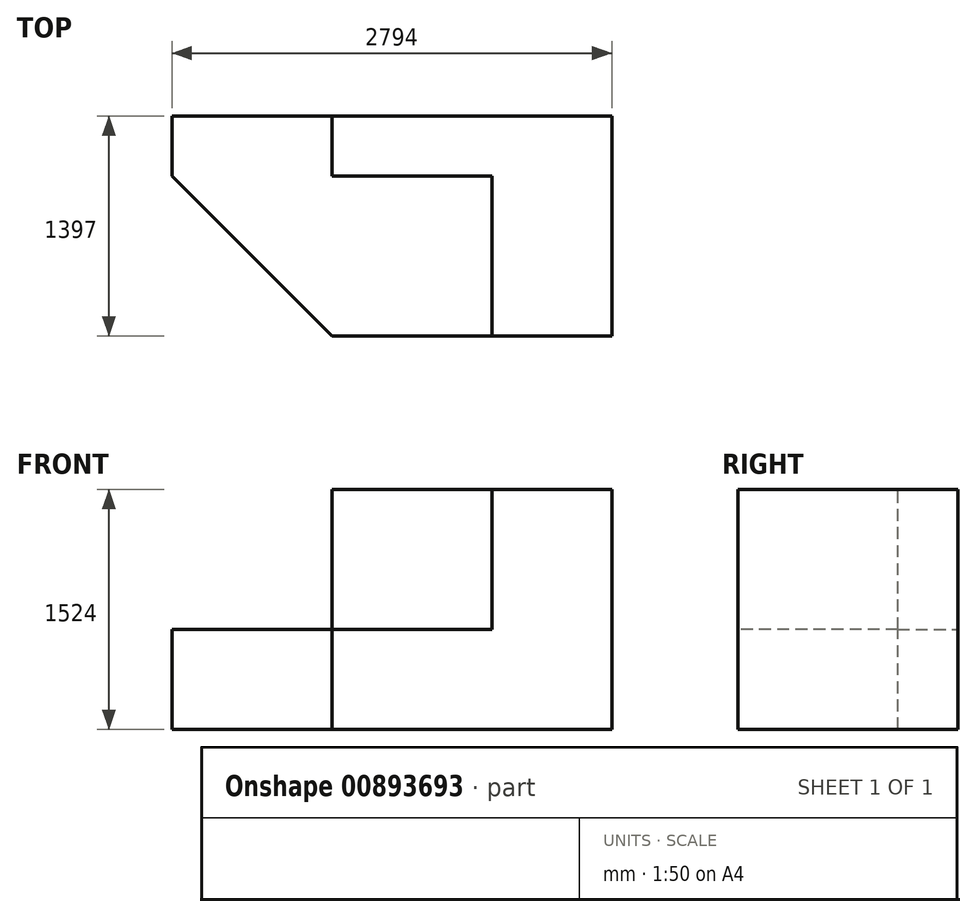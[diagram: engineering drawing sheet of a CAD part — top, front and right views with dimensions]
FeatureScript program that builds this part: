
annotation { "Feature Type Name" : "Feature", "Feature Type Description" : "" }
export const myFeature = defineFeature(function(context is Context, id is Id, definition is map)
    precondition{}
    {
        {
            var Q0;
            Q0=qCreatedBy(makeId("Front.planeOp"),FACE);
            var sketch = newSketch(context, id + "F0", { "sketchPlane" : qUnion([Q0])});
            skLineSegment(sketch, "E0", {"start": v(-1319.03, -475.08) * mm, "end": v(1474.97, -475.08) * mm});
            skLineSegment(sketch, "E1", {"start": v(-1319.03, -475.08) * mm, "end": v(-1319.03, 159.92) * mm});
            skLineSegment(sketch, "E2", {"start": v(1474.97, -475.08) * mm, "end": v(1474.97, 1048.92) * mm});
            skLineSegment(sketch, "E3", {"start": v(1474.97, 1048.92) * mm, "end": v(712.97, 1048.92) * mm});
            skLineSegment(sketch, "E4", {"start": v(712.97, 1048.92) * mm, "end": v(-303.03, 1048.92) * mm});
            skLineSegment(sketch, "E5", {"start": v(-1319.03, 159.92) * mm, "end": v(-303.03, 159.92) * mm});
            skLineSegment(sketch, "E6", {"start": v(-303.03, 159.92) * mm, "end": v(-303.03, 1048.92) * mm});
            skLineSegment(sketch, "E7", {"start": v(712.97, 1048.92) * mm, "end": v(712.97, 159.92) * mm});
            skLineSegment(sketch, "E8", {"start": v(712.97, 159.92) * mm, "end": v(-303.03, 159.92) * mm});
            skSolve(sketch);
        }
        {
            var Q0;
            Q0=makeQuery(id+"F0.imprint","IMPRINT",FACE,{"disambiguationData":[TD([[makeQuery(id+"F0.imprint","IMPRINT",EDGE,{"derivedFrom":sQuery(id+"F0.wireOp",EDGE,"E4")}),1.0]])]});
            var Q1;
            Q1=makeQuery(id+"F0.imprint","IMPRINT",FACE,{"disambiguationData":[TD([[makeQuery(id+"F0.imprint","IMPRINT",EDGE,{"derivedFrom":sQuery(id+"F0.wireOp",EDGE,"E0")}),1.0]])]});
            extrude(context, id + "F1", {"entities" : qUnion([Q0, Q1]), "depth" : 1397 * mm, "offsetDistance" : 25.4 * mm});
        }
        {
            var Q0;
            Q0=makeQuery(id+"F1.opExtrude","CAP_FACE",FACE,{"disambiguationData":[OSD([sQuery(id+"F0.wireOp",EDGE,"E0"),sQuery(id+"F0.wireOp",EDGE,"E1"),sQuery(id+"F0.wireOp",EDGE,"E2"),sQuery(id+"F0.wireOp",EDGE,"E3"),sQuery(id+"F0.wireOp",EDGE,"E4"),sQuery(id+"F0.wireOp",EDGE,"E5"),sQuery(id+"F0.wireOp",EDGE,"E6")])],"isStart":false});
            var sketch = newSketch(context, id + "F2", { "sketchPlane" : qUnion([Q0])});
            skLineSegment(sketch, "E9", {"start": v(-303.03, 159.92) * mm, "end": v(712.97, 159.92) * mm});
            skLineSegment(sketch, "E10", {"start": v(712.97, 159.92) * mm, "end": v(712.97, 1048.92) * mm});
            skLineSegment(sketch, "E11", {"start": v(712.97, 1048.92) * mm, "end": v(-303.03, 1048.92) * mm});
            skLineSegment(sketch, "E12", {"start": v(-303.03, 1048.92) * mm, "end": v(-303.03, 159.92) * mm});
            skSolve(sketch);
        }
        {
            var Q0;
            Q0=makeQuery(id+"F1.opExtrude","SWEPT_FACE",FACE,{"disambiguationData":[OSD([sQuery(id+"F0.wireOp",EDGE,"E3"),sQuery(id+"F0.wireOp",EDGE,"E4")])]});
            var sketch = newSketch(context, id + "F3", { "sketchPlane" : qUnion([Q0])});
            skLineSegment(sketch, "E13", {"start": v(1474.97, -1397) * mm, "end": v(1474.97, -381) * mm});
            skLineSegment(sketch, "E14", {"start": v(1474.97, -381) * mm, "end": v(712.97, -381) * mm});
            skLineSegment(sketch, "E15", {"start": v(712.97, -381) * mm, "end": v(712.97, -1397) * mm});
            skLineSegment(sketch, "E16", {"start": v(712.97, -381) * mm, "end": v(-303.03, -381) * mm});
            skSolve(sketch);
        }
        {
            var Q0;
            Q0 = qSketchRegion(id + "F3", true);
            var Q1;
            Q1=makeQuery(id+"F2.imprint","IMPRINT",FACE,{"disambiguationData":[TD([[makeQuery(id+"F2.imprint","IMPRINT",EDGE,{"derivedFrom":sQuery(id+"F2.wireOp",EDGE,"E9")}),1.0]])]});
            extrude(context, id + "F4", {"entities" : qUnion([Q0, Q1]), "operationType" : NewBodyOperationType.REMOVE, "oppositeDirection" : true, "depth" : 1016 * mm, "offsetDistance" : 25.4 * mm});
        }
        {
            var Q0;
            Q0=makeQuery(id+"F4.boolean.opBoolean","MERGE",FACE,{"derivedFrom":[makeQuery(id+"F1.opExtrude","SWEPT_FACE",FACE,{"disambiguationData":[OSD([sQuery(id+"F0.wireOp",EDGE,"E5")])]})],"fromTools":[makeQuery(id+"F4.opExtrude","SWEPT_FACE",FACE,{"disambiguationData":[OSD([sQuery(id+"F2.wireOp",EDGE,"E9")])]})]});
            var sketch = newSketch(context, id + "F5", { "sketchPlane" : qUnion([Q0])});
            skLineSegment(sketch, "E17", {"start": v(-1319.03, -381) * mm, "end": v(-303.03, -1397) * mm});
            skLineSegment(sketch, "E18", {"start": v(-1319.03, -381) * mm, "end": v(-1319.03, -1397) * mm});
            skLineSegment(sketch, "E19", {"start": v(-1319.03, -1397) * mm, "end": v(-303.03, -1397) * mm});
            skSolve(sketch);
        }
        {
            var Q0;
            Q0=makeQuery(id+"F5.imprint","IMPRINT",FACE,{"disambiguationData":[TD([[makeQuery(id+"F5.imprint","IMPRINT",EDGE,{"derivedFrom":sQuery(id+"F5.wireOp",EDGE,"E17")}),-1.0]])]});
            extrude(context, id + "F6", {"entities" : qUnion([Q0]), "operationType" : NewBodyOperationType.REMOVE, "oppositeDirection" : true, "depth" : 1419.86 * mm, "offsetDistance" : 25.4 * mm});
        }
    });
